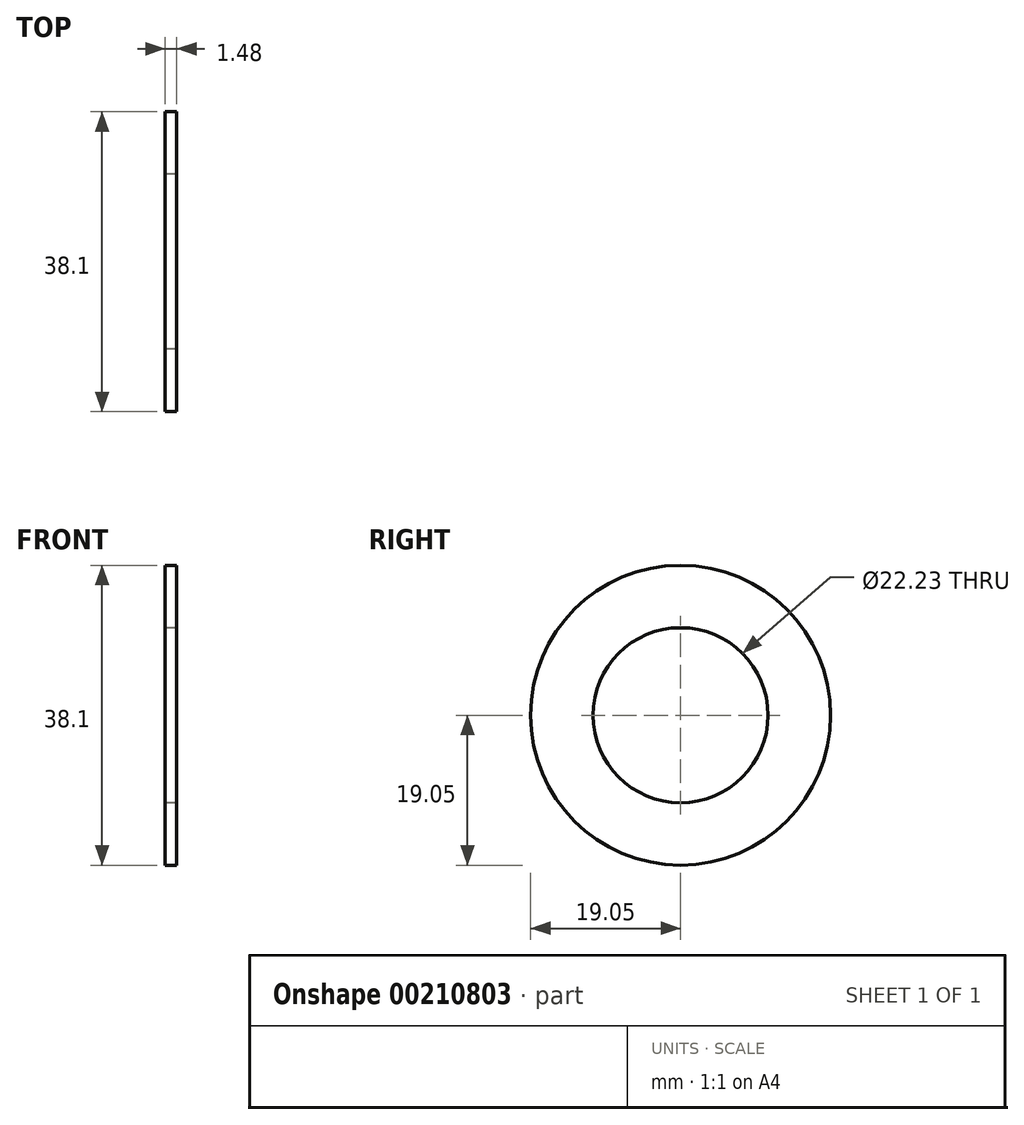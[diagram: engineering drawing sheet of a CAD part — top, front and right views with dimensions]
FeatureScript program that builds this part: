
annotation { "Feature Type Name" : "Feature", "Feature Type Description" : "" }
export const myFeature = defineFeature(function(context is Context, id is Id, definition is map)
    precondition{}
    {
        {
            var Q0;
            Q0=qCreatedBy(makeId("Right.planeOp"),FACE);
            var sketch = newSketch(context, id + "F0", { "sketchPlane" : qUnion([Q0])});
            skCircle(sketch, "E0", {"center": v(0, 0) * mm, "radius": 11.11 * mm});
            skCircle(sketch, "E1", {"center": v(0, 0) * mm, "radius": 19.05 * mm});
            skSolve(sketch);
        }
        {
            var Q0;
            Q0 = qSketchRegion(id + "F0", true);
            extrude(context, id + "F1", {"entities" : qUnion([Q0]), "endBound" : BoundingType.SYMMETRIC, "depth" : 1.49 * mm});
        }
    });
